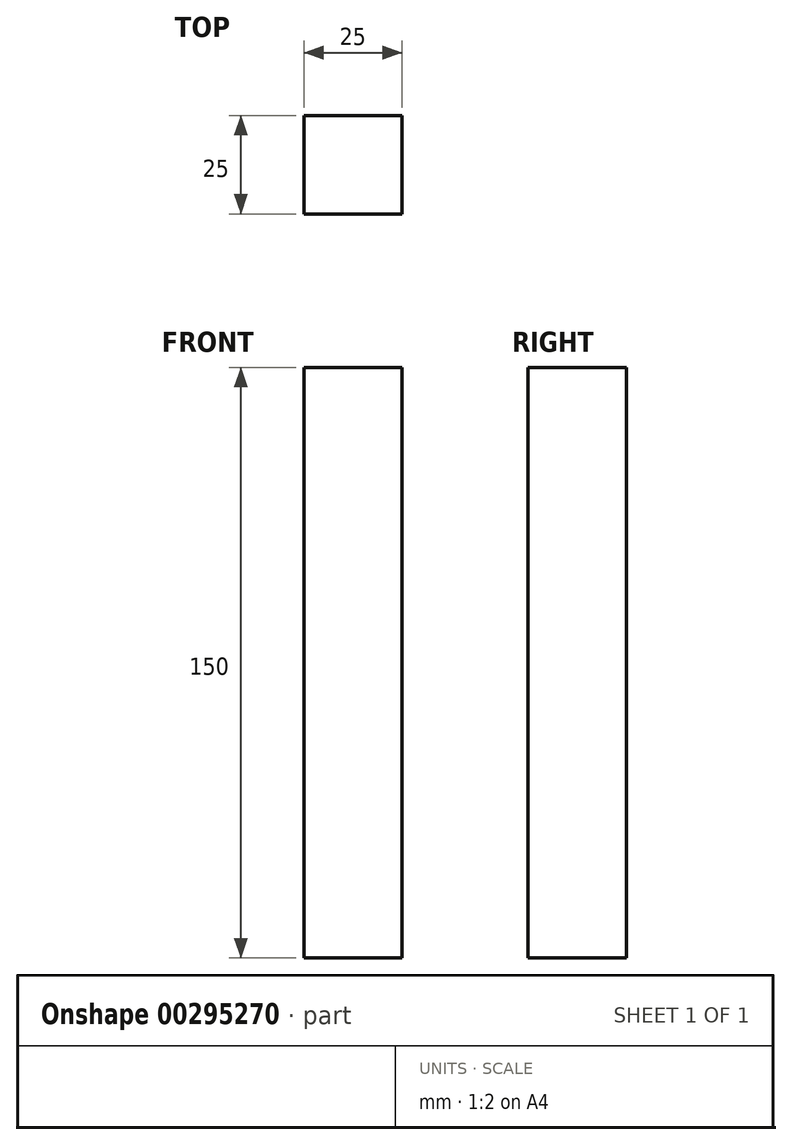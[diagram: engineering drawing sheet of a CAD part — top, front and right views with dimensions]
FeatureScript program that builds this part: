
annotation { "Feature Type Name" : "Feature", "Feature Type Description" : "" }
export const myFeature = defineFeature(function(context is Context, id is Id, definition is map)
    precondition{}
    {
        {
            var Q0;
            Q0=qCreatedBy(makeId("Front.planeOp"),FACE);
            var sketch = newSketch(context, id + "F0", { "sketchPlane" : qUnion([Q0])});
            skLineSegment(sketch, "E0.bottom", {"start": v(0, 0) * mm, "end": v(25, 0) * mm});
            skLineSegment(sketch, "E0.top", {"start": v(0, 150) * mm, "end": v(25, 150) * mm});
            skLineSegment(sketch, "E0.left", {"start": v(0, 0) * mm, "end": v(0, 150) * mm});
            skLineSegment(sketch, "E0.right", {"start": v(25, 0) * mm, "end": v(25, 150) * mm});
            skSolve(sketch);
        }
        {
            var Q0;
            Q0=qSketchRegion(id+"F0",true);
            extrude(context, id + "F1", {"entities" : qUnion([Q0]), "depth" : 25 * mm});
        }
    });
